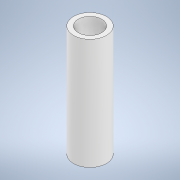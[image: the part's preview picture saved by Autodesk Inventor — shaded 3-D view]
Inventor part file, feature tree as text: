
AUTODESK INVENTOR PART (.ipt)
format: ipt  version: 2021 (Build 250183000, 183)  size: 97,792 bytes
history: native  units: mm
features: extrude x1, sketch x1
ambient origin geometry x8: Origin, YZ Plane, XZ Plane, XY Plane, X Axis, Y Axis, Z Axis, Center Point
bodies: Solid1 (feature_tree)
feature tree (2):
  extrude  "Extrusion1"  Depth=90.0mm
  sketch  "Sketch1"  dims[d0=26.67mm d1=19.05mm d2=90.0mm d3=0.0mm]
